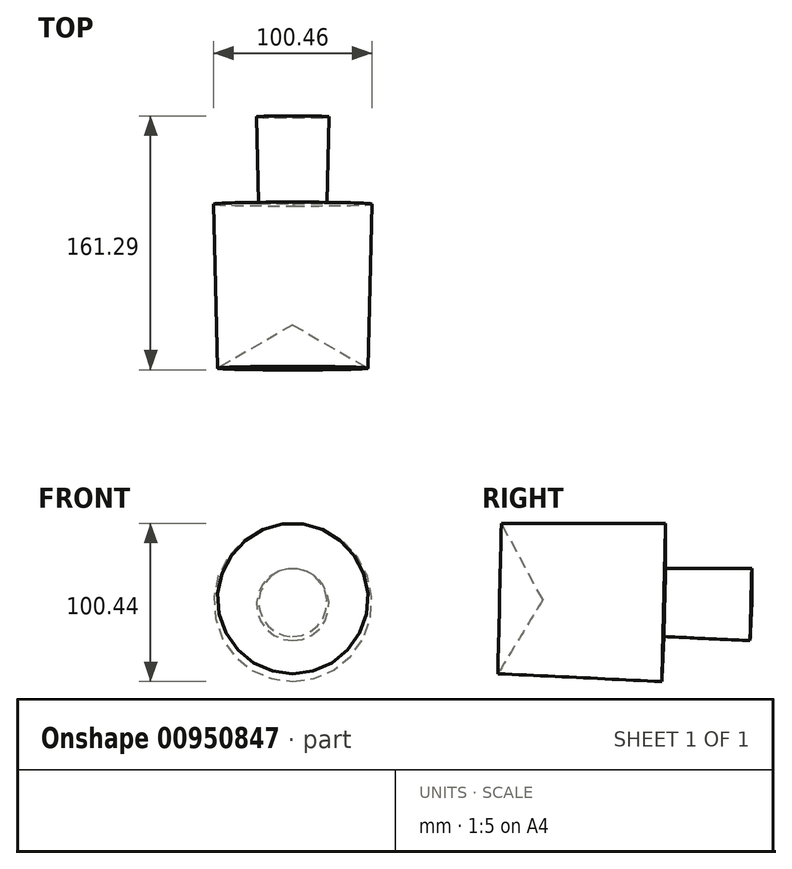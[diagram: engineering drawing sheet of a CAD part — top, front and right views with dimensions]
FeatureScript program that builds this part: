
annotation { "Feature Type Name" : "Feature", "Feature Type Description" : "" }
export const myFeature = defineFeature(function(context is Context, id is Id, definition is map)
    precondition{}
    {
        {
            var Q0;
            Q0=qCreatedBy(makeId("Right.planeOp"),FACE);
            var sketch = newSketch(context, id + "F0", { "sketchPlane" : qUnion([Q0])});
            skLineSegment(sketch, "E0", {"start": v(-26.59, 16.74) * mm, "end": v(-52.93, 65.14) * mm});
            skLineSegment(sketch, "E1", {"start": v(-52.93, 65.14) * mm, "end": v(51.34, 65.14) * mm});
            skLineSegment(sketch, "E2", {"start": v(51.34, 65.14) * mm, "end": v(51.34, 36.56) * mm});
            skLineSegment(sketch, "E3", {"start": v(51.34, 36.56) * mm, "end": v(106.1, 36.56) * mm});
            skLineSegment(sketch, "E4", {"start": v(106.1, 36.56) * mm, "end": v(106.1, 13.6) * mm});
            skLineSegment(sketch, "E5", {"start": v(-26.59, 16.74) * mm, "end": v(106.1, 13.6) * mm});
            skSolve(sketch);
        }
        {
            var Q0;
            Q0=makeQuery(id+"F0.imprint","IMPRINT",FACE,{"disambiguationData":[TD([[makeQuery(id+"F0.imprint","IMPRINT",EDGE,{"derivedFrom":sQuery(id+"F0.wireOp",EDGE,"E0")}),-1.0]])]});
            var Q1;
            Q1=sQuery(id+"F0.wireOp",EDGE,"E5");
            revolve(context, id + "F1", {"surfaceOperationType" : NewSurfaceOperationType.NEW, "entities" : qUnion([Q0]), "axis" : qUnion([Q1]), "revolveType" : RevolveType.FULL});
        }
    });
